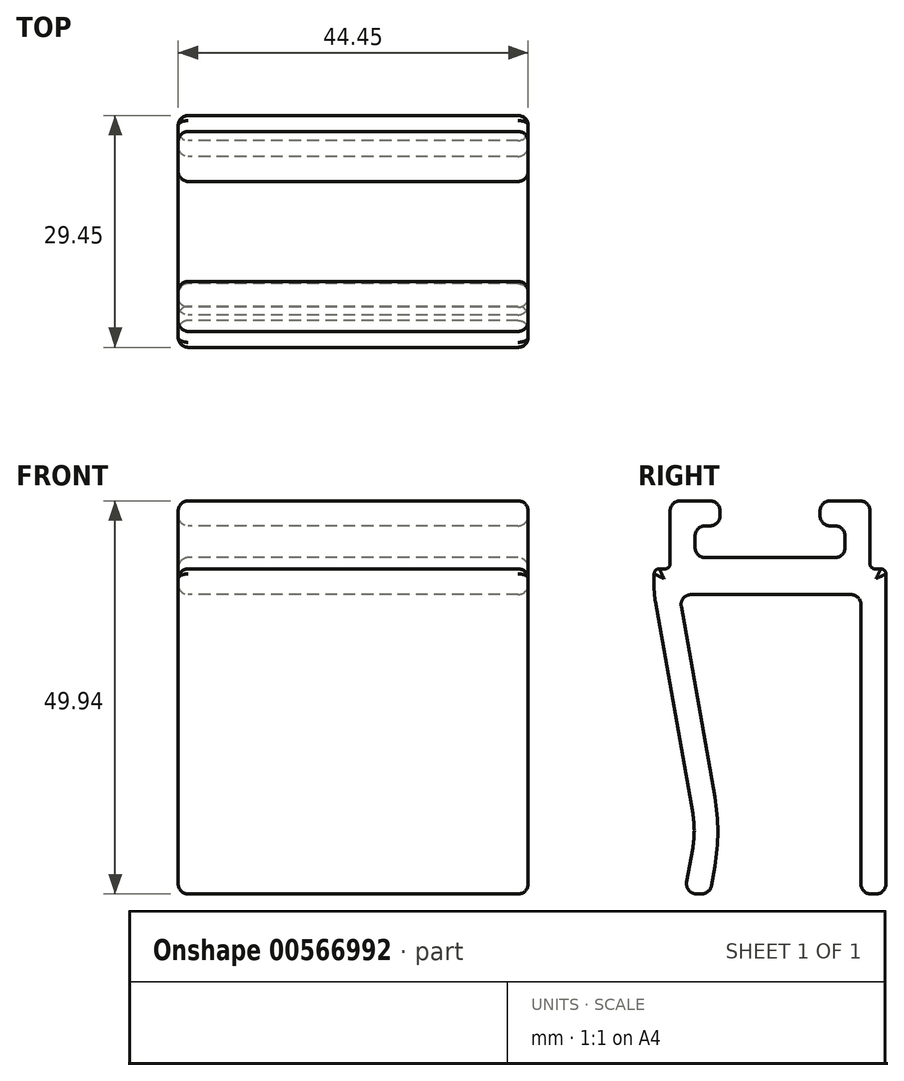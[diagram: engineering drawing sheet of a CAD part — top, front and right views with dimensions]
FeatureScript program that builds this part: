
annotation { "Feature Type Name" : "Feature", "Feature Type Description" : "" }
export const myFeature = defineFeature(function(context is Context, id is Id, definition is map)
    precondition{}
    {
        {
            var Q0;
            Q0=qCreatedBy(makeId("Right.planeOp"),FACE);
            var sketch = newSketch(context, id + "F0", { "sketchPlane" : qUnion([Q0])});
            skLineSegment(sketch, "E0.bottom", {"start": v(13.34, -24.97) * mm, "end": v(12.7, -24.97) * mm});
            skLineSegment(sketch, "E0.top", {"start": v(11.31, 24.97) * mm, "end": v(7.5, 24.97) * mm});
            skLineSegment(sketch, "E0.left", {"start": v(14.6, -23.7) * mm, "end": v(14.6, 15.7) * mm});
            skPoint(sketch, "E0.middle", {"position": v(0, 0) * mm});
            skLineSegment(sketch, "E1.top", {"start": v(-10.15, 13.06) * mm, "end": v(10.16, 13.06) * mm});
            skLineSegment(sketch, "E1.right", {"start": v(11.43, -23.7) * mm, "end": v(11.43, 11.8) * mm});
            skLineSegment(sketch, "E2.bottom", {"start": v(8.14, 17.75) * mm, "end": v(-8.37, 17.75) * mm});
            skLineSegment(sketch, "E2.top", {"start": v(8.14, 21.8) * mm, "end": v(7.5, 21.8) * mm});
            skLineSegment(sketch, "E2.left", {"start": v(9.4, 19.02) * mm, "end": v(9.4, 20.52) * mm});
            skLineSegment(sketch, "E2.right", {"start": v(-9.64, 19.02) * mm, "end": v(-9.64, 20.52) * mm});
            skPoint(sketch, "E2.middle", {"position": v(-0.12, 19.77) * mm});
            skPoint(sketch, "E2.middle.positionSnap0", {"position": v(-0.12, 13.06) * mm});
            skPoint(sketch, "E2.centerSnap0", {"position": v(-0.12, 13.06) * mm});
            skLineSegment(sketch, "E3.left", {"start": v(6.23, 23.7) * mm, "end": v(6.23, 23.06) * mm});
            skLineSegment(sketch, "E3.right", {"start": v(-6.47, 23.7) * mm, "end": v(-6.47, 23.06) * mm});
            skPoint(sketch, "E3.middle", {"position": v(-0.12, 21.8) * mm});
            skLineSegment(sketch, "E4.trimOffspring", {"start": v(-7.74, 21.8) * mm, "end": v(-8.37, 21.8) * mm});
            skLineSegment(sketch, "E5.trimOffspring", {"start": v(-7.74, 24.97) * mm, "end": v(-11.55, 24.97) * mm});
            skPoint(sketch, "E3.top.end.orphan", {"position": v(-6.47, 18.62) * mm});
            skPoint(sketch, "E6.orphan", {"position": v(6.23, 18.62) * mm});
            skLineSegment(sketch, "E7.top", {"start": v(-14.2, 16.33) * mm, "end": v(-13.45, 16.33) * mm});
            skLineSegment(sketch, "E7.right", {"start": v(-12.82, 23.7) * mm, "end": v(-12.82, 16.97) * mm});
            skPoint(sketch, "E8.orphan", {"position": v(-14.6, 24.97) * mm});
            skLineSegment(sketch, "E9.top", {"start": v(13.97, 16.33) * mm, "end": v(13.22, 16.33) * mm});
            skLineSegment(sketch, "E9.right", {"start": v(12.58, 23.7) * mm, "end": v(12.58, 16.97) * mm});
            skPoint(sketch, "E10.orphan", {"position": v(14.6, 24.97) * mm});
            skPoint(sketch, "E11.visualSharp", {"position": v(-6.47, 21.8) * mm});
            skArc(sketch, "E11.filletArc", {"start": v(-7.74, 21.8) * mm, "mid": v(-6.84, 22.16) * mm, "end": v(-6.47, 23.06) * mm});
            skPoint(sketch, "E12.visualSharp", {"position": v(6.23, 21.8) * mm});
            skArc(sketch, "E12.filletArc", {"start": v(6.23, 23.06) * mm, "mid": v(6.6, 22.16) * mm, "end": v(7.5, 21.8) * mm});
            skPoint(sketch, "E13.visualSharp", {"position": v(6.23, 24.97) * mm});
            skArc(sketch, "E13.filletArc", {"start": v(7.5, 24.97) * mm, "mid": v(6.6, 24.6) * mm, "end": v(6.23, 23.7) * mm});
            skPoint(sketch, "E14.visualSharp", {"position": v(-6.47, 24.97) * mm});
            skArc(sketch, "E14.filletArc", {"start": v(-6.47, 23.7) * mm, "mid": v(-6.84, 24.6) * mm, "end": v(-7.74, 24.97) * mm});
            skPoint(sketch, "E15.visualSharp", {"position": v(-12.82, 24.97) * mm});
            skArc(sketch, "E15.filletArc", {"start": v(-11.55, 24.97) * mm, "mid": v(-12.44, 24.6) * mm, "end": v(-12.82, 23.7) * mm});
            skPoint(sketch, "E16.visualSharp", {"position": v(12.58, 24.97) * mm});
            skArc(sketch, "E16.filletArc", {"start": v(12.58, 23.7) * mm, "mid": v(12.21, 24.6) * mm, "end": v(11.31, 24.97) * mm});
            skPoint(sketch, "E17.visualSharp", {"position": v(-9.64, 17.75) * mm});
            skArc(sketch, "E17.filletArc", {"start": v(-9.64, 19.02) * mm, "mid": v(-9.27, 18.13) * mm, "end": v(-8.37, 17.75) * mm});
            skPoint(sketch, "E18.visualSharp", {"position": v(9.4, 17.75) * mm});
            skArc(sketch, "E18.filletArc", {"start": v(8.14, 17.75) * mm, "mid": v(9.04, 18.13) * mm, "end": v(9.4, 19.02) * mm});
            skPoint(sketch, "E19.visualSharp", {"position": v(14.6, 16.33) * mm});
            skPoint(sketch, "E20.visualSharp", {"position": v(-12.82, 16.33) * mm});
            skPoint(sketch, "E21.visualSharp", {"position": v(-14.22, 16.33) * mm});
            skPoint(sketch, "E22.visualSharp", {"position": v(11.43, -24.97) * mm});
            skArc(sketch, "E22.filletArc", {"start": v(11.43, -23.7) * mm, "mid": v(11.8, -24.6) * mm, "end": v(12.7, -24.97) * mm});
            skPoint(sketch, "E23.visualSharp", {"position": v(14.6, -24.97) * mm});
            skArc(sketch, "E23.filletArc", {"start": v(13.34, -24.97) * mm, "mid": v(14.23, -24.6) * mm, "end": v(14.6, -23.7) * mm});
            skPoint(sketch, "E24.visualSharp", {"position": v(-9.64, 21.8) * mm});
            skArc(sketch, "E24.filletArc", {"start": v(-8.37, 21.8) * mm, "mid": v(-9.27, 21.42) * mm, "end": v(-9.64, 20.52) * mm});
            skPoint(sketch, "E25.visualSharp", {"position": v(9.4, 21.8) * mm});
            skArc(sketch, "E25.filletArc", {"start": v(9.4, 20.52) * mm, "mid": v(9.04, 21.42) * mm, "end": v(8.14, 21.8) * mm});
            skLineSegment(sketch, "E26", {"start": v(-11.4, 11.57) * mm, "end": v(-7.13, -12.65) * mm});
            skLineSegment(sketch, "E27", {"start": v(-14.84, 15.7) * mm, "end": v(-14.84, 13.95) * mm});
            skLineSegment(sketch, "E28", {"start": v(-14.68, 12.19) * mm, "end": v(-9.94, -14.72) * mm});
            skPoint(sketch, "E29.visualSharp", {"position": v(-11.66, 13.06) * mm});
            skArc(sketch, "E29.filletArc", {"start": v(-10.15, 13.06) * mm, "mid": v(-11.12, 12.6) * mm, "end": v(-11.4, 11.57) * mm});
            skPoint(sketch, "E30.visualSharp", {"position": v(11.43, 13.06) * mm});
            skArc(sketch, "E30.filletArc", {"start": v(11.43, 11.8) * mm, "mid": v(11.06, 12.69) * mm, "end": v(10.16, 13.06) * mm});
            skLineSegment(sketch, "E31", {"start": v(-7.13, -21.47) * mm, "end": v(-7.56, -23.92) * mm});
            skLineSegment(sketch, "E32", {"start": v(-9.94, -19.13) * mm, "end": v(-10.7, -23.48) * mm});
            skPoint(sketch, "E33.visualSharp", {"position": v(-14.84, 16.33) * mm});
            skArc(sketch, "E33.filletArc", {"start": v(-14.2, 16.33) * mm, "mid": v(-14.65, 16.15) * mm, "end": v(-14.84, 15.7) * mm});
            skPoint(sketch, "E34.visualSharp", {"position": v(-14.84, 13.06) * mm});
            skArc(sketch, "E34.filletArc", {"start": v(-14.84, 13.95) * mm, "mid": v(-14.8, 13.06) * mm, "end": v(-14.68, 12.19) * mm});
            skLineSegment(sketch, "E35", {"start": v(-12.82, 16.33) * mm, "end": v(12.58, 16.33) * mm, "construction": true});
            skPoint(sketch, "E36.visualSharp", {"position": v(12.58, 16.33) * mm});
            skArc(sketch, "E36.filletArc", {"start": v(12.58, 16.97) * mm, "mid": v(12.77, 16.52) * mm, "end": v(13.22, 16.33) * mm});
            skArc(sketch, "E37.filletArc", {"start": v(-13.45, 16.33) * mm, "mid": v(-13, 16.52) * mm, "end": v(-12.82, 16.97) * mm});
            skArc(sketch, "E38.filletArc", {"start": v(14.6, 15.7) * mm, "mid": v(14.42, 16.15) * mm, "end": v(13.97, 16.33) * mm});
            skLineSegment(sketch, "E39", {"start": v(-9.45, -24.97) * mm, "end": v(-8.8, -24.97) * mm});
            skPoint(sketch, "E40.visualSharp", {"position": v(-6.35, -17.06) * mm});
            skArc(sketch, "E40.filletArc", {"start": v(-7.13, -21.47) * mm, "mid": v(-6.74, -17.06) * mm, "end": v(-7.13, -12.65) * mm});
            skPoint(sketch, "E41.visualSharp", {"position": v(-9.55, -16.93) * mm});
            skArc(sketch, "E41.filletArc", {"start": v(-9.94, -19.13) * mm, "mid": v(-9.75, -16.93) * mm, "end": v(-9.94, -14.72) * mm});
            skPoint(sketch, "E42.visualSharp", {"position": v(-10.97, -24.97) * mm});
            skArc(sketch, "E42.filletArc", {"start": v(-10.7, -23.48) * mm, "mid": v(-10.43, -24.51) * mm, "end": v(-9.45, -24.97) * mm});
            skPoint(sketch, "E43.visualSharp", {"position": v(-7.74, -24.97) * mm});
            skArc(sketch, "E43.filletArc", {"start": v(-8.8, -24.97) * mm, "mid": v(-8, -24.67) * mm, "end": v(-7.56, -23.92) * mm});
            skSolve(sketch);
        }
        {
            var Q0;
            Q0=qSketchRegion(id+"F0",true);
            extrude(context, id + "F1", {"entities" : qUnion([Q0]), "depth" : 44.45 * mm, "offsetDistance" : 25.4 * mm});
        }
        {
            var Q0;
            Q0=makeQuery(id+"F1.opExtrude","CAP_EDGE",EDGE,{"disambiguationData":[OSD([sQuery(id+"F0.wireOp",EDGE,"E7.right")])],"isStart":false});
            var Q1;
            Q1=makeQuery(id+"F1.opExtrude","CAP_EDGE",EDGE,{"disambiguationData":[OSD([sQuery(id+"F0.wireOp",EDGE,"E5.trimOffspring")])],"isStart":false});
            var Q2;
            Q2=makeQuery(id+"F1.opExtrude","CAP_EDGE",EDGE,{"disambiguationData":[OSD([sQuery(id+"F0.wireOp",EDGE,"E2.bottom")])],"isStart":true});
            var Q3;
            Q3=makeQuery(id+"F1.opExtrude","CAP_EDGE",EDGE,{"disambiguationData":[OSD([sQuery(id+"F0.wireOp",EDGE,"E1.top")])],"isStart":true});
            var Q4;
            Q4=makeQuery(id+"F1.opExtrude","CAP_EDGE",EDGE,{"disambiguationData":[OSD([sQuery(id+"F0.wireOp",EDGE,"E1.top")])],"isStart":false});
            fillet(context, id + "F2", {"entities" : qUnion([Q0, Q1, Q2, Q3, Q4]), "radius" : 1.27 * mm, "tangentPropagation" : true, "allowEdgeOverflow" : false});
        }
    });
